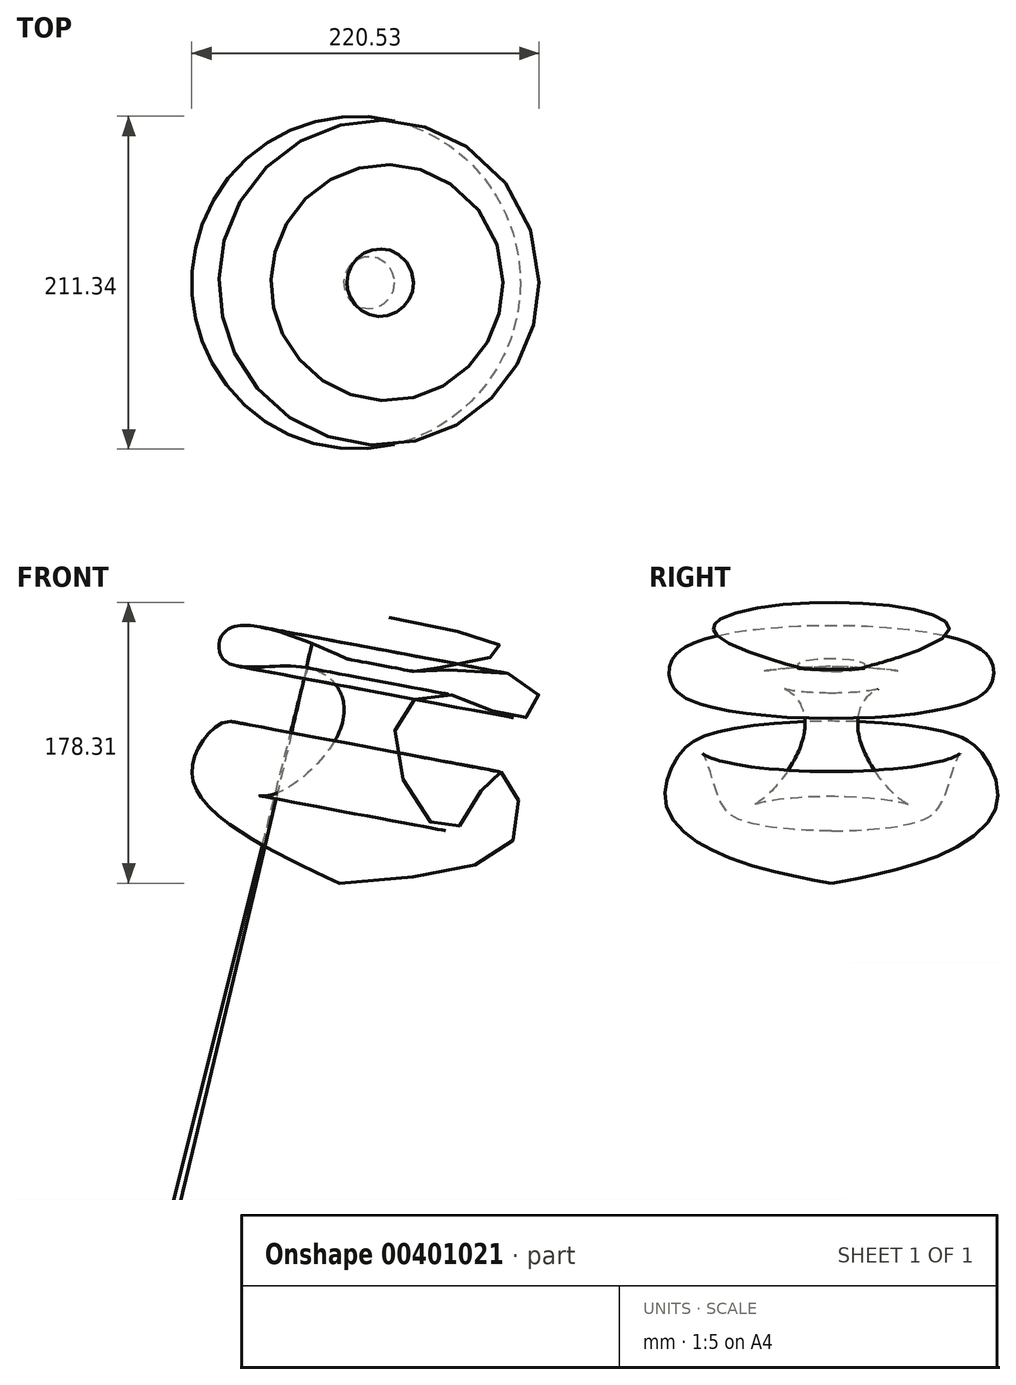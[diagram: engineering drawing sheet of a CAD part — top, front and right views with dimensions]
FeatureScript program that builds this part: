
annotation { "Feature Type Name" : "Feature", "Feature Type Description" : "" }
export const myFeature = defineFeature(function(context is Context, id is Id, definition is map)
    precondition{}
    {
        {
            var Q0;
            Q0=qCreatedBy(makeId("Front.planeOp"),FACE);
            var sketch = newSketch(context, id + "F0", { "sketchPlane" : qUnion([Q0])});
            skLineSegment(sketch, "E0", {"start": v(-12.54, 100.88) * mm, "end": v(-44.22, -67.99) * mm});
            skLineSegment(sketch, "E1", {"start": v(-12.54, 100.88) * mm, "end": v(-18.47, 69.3) * mm});
            skFitSpline(sketch, "E2", {"points": [v(-12.54, 100.88) * mm, v(58.38, 78.25) * mm, v(2.88, 66.54) * mm, v(77.16, 59.76) * mm, v(75, 37.49) * mm, v(21.02, 52.58) * mm, v(-9.39, 23.54) * mm, v(27.32, -34.48) * mm, v(55.57, 2.8) * mm, v(69.57, -33.79) * mm, v(-44.22, -67.99) * mm], "startDerivative": vector(1060.3, -207.17) * mm, "endDerivative": vector(-1103.25, -76.67) * mm});
            skSolve(sketch);
        }
        {
            var Q0;
            Q0=makeQuery(id+"F0.imprint","IMPRINT",FACE,{"disambiguationData":[TD([[makeQuery(id+"F0.imprint","IMPRINT",EDGE,{"derivedFrom":sQuery(id+"F0.wireOp",EDGE,"E0")}),1.0]])]});
            var Q1;
            Q1=sQuery(id+"F0.wireOp",EDGE,"E0");
            revolve(context, id + "F1", {"entities" : qUnion([Q0]), "axis" : qUnion([Q1]), "revolveType" : RevolveType.FULL});
        }
    });
